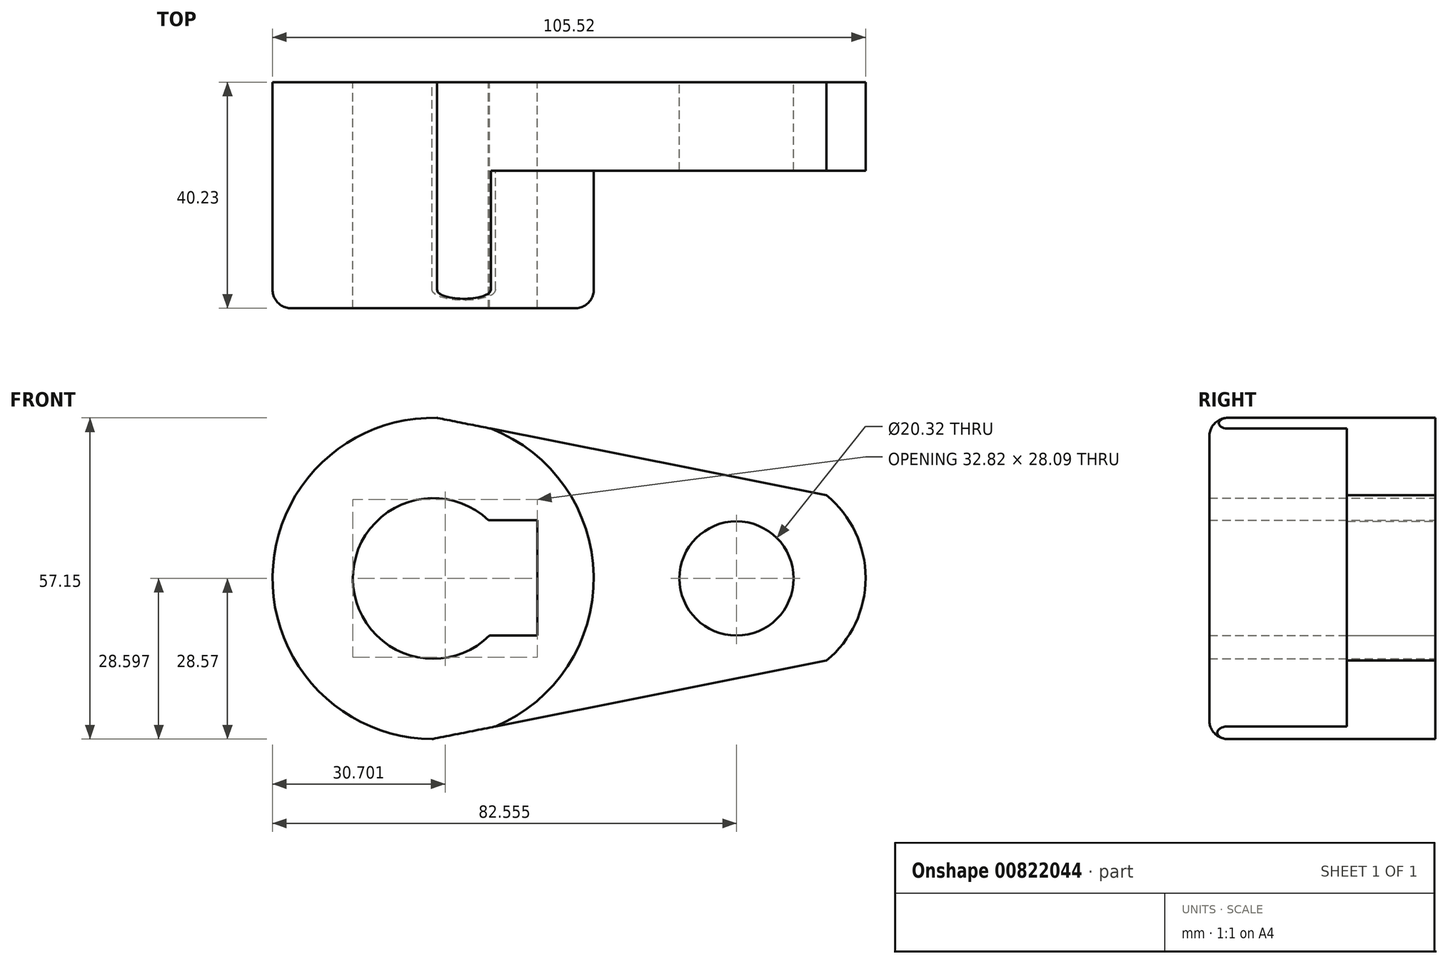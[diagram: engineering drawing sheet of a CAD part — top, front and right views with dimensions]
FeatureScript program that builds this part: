
annotation { "Feature Type Name" : "Feature", "Feature Type Description" : "" }
export const myFeature = defineFeature(function(context is Context, id is Id, definition is map)
    precondition{}
    {
        {
            var Q0;
            Q0=qCreatedBy(makeId("Front.planeOp"),FACE);
            var sketch = newSketch(context, id + "F0", { "sketchPlane" : qUnion([Q0])});
            skCircle(sketch, "E0", {"center": v(-57.07, 0) * mm, "radius": 28.58 * mm});
            skArc(sketch, "E1", {"start": v(-47.23, 10.36) * mm, "mid": v(-71.36, -0.15) * mm, "end": v(-47.02, -10.15) * mm});
            skLineSegment(sketch, "E2", {"start": v(-47.23, 10.36) * mm, "end": v(-38.54, 10.36) * mm});
            skLineSegment(sketch, "E3", {"start": v(-38.54, 10.36) * mm, "end": v(-38.54, -10.15) * mm});
            skLineSegment(sketch, "E4", {"start": v(-38.54, -10.15) * mm, "end": v(-47.02, -10.15) * mm});
            skCircle(sketch, "E5", {"center": v(-3.1, 0) * mm, "radius": 10.16 * mm});
            skLineSegment(sketch, "E6", {"start": v(-56.4, 28.57) * mm, "end": v(12.93, 14.8) * mm});
            skLineSegment(sketch, "E7", {"start": v(-57.24, -28.57) * mm, "end": v(12.93, -14.6) * mm});
            skLineSegment(sketch, "E8.trimOffspring", {"start": v(-3.5, -10.15) * mm, "end": v(-2.7, -10.15) * mm, "construction": true});
            skArc(sketch, "E9", {"start": v(12.93, -14.6) * mm, "mid": v(19.87, 0.1) * mm, "end": v(12.93, 14.8) * mm});
            skPoint(sketch, "E10.end.orphan", {"position": v(35.33, 10.36) * mm});
            skPoint(sketch, "E11.orphan", {"position": v(35.33, -10.15) * mm});
            skSolve(sketch);
        }
        {
            var Q0;
            {var subQ0=sQuery(id+"F0.wireOp",EDGE,"E6");var subQ1=sQuery(id+"F0.wireOp",EDGE,"E0");var subQ2=makeQuery(id+"F0.imprint","INTERSECT",VERTEX,{"disambiguationData":[OD(0.0)],"derivedFrom":[subQ1,subQ0]});Q0=makeQuery(id+"F0.imprint","IMPRINT",FACE,{"disambiguationData":[TD([[makeQuery(id+"F0.imprint","IMPRINT",EDGE,{"disambiguationData":[TD([[subQ2,1.0]])],"derivedFrom":subQ1}),1.0]])]});}
            var Q1;
            {var subQ0=sQuery(id+"F0.wireOp",EDGE,"E7");var subQ1=sQuery(id+"F0.wireOp",EDGE,"E0");var subQ2=makeQuery(id+"F0.imprint","INTERSECT",VERTEX,{"disambiguationData":[OD(0.0)],"derivedFrom":[subQ1,subQ0]});Q1=makeQuery(id+"F0.imprint","IMPRINT",FACE,{"disambiguationData":[TD([[makeQuery(id+"F0.imprint","IMPRINT",EDGE,{"disambiguationData":[TD([[subQ2,-1.0]])],"derivedFrom":subQ1}),1.0]])]});}
            var Q2;
            Q2=makeQuery(id+"F0.imprint","IMPRINT",FACE,{"disambiguationData":[TD([[makeQuery(id+"F0.imprint","IMPRINT",EDGE,{"derivedFrom":sQuery(id+"F0.wireOp",EDGE,"E1")}),-1.0]])]});
            extrude(context, id + "F1", {"entities" : qUnion([Q0, Q1, Q2]), "depth" : 40.23 * mm, "offsetDistance" : 25.4 * mm});
        }
        {
            var Q0;
            Q0=makeQuery(id+"F0.imprint","IMPRINT",FACE,{"disambiguationData":[TD([[makeQuery(id+"F0.imprint","IMPRINT",EDGE,{"derivedFrom":sQuery(id+"F0.wireOp",EDGE,"E5")}),-1.0]])]});
            extrude(context, id + "F2", {"entities" : qUnion([Q0]), "operationType" : NewBodyOperationType.ADD, "depth" : 15.77 * mm, "offsetDistance" : 25.4 * mm});
        }
        {
            var Q0;
            Q0=makeQuery(id+"F1.opExtrude","CAP_EDGE",EDGE,{"disambiguationData":[OSD([sQuery(id+"F0.wireOp",EDGE,"E0")])],"isStart":false});
            fillet(context, id + "F3", {"entities" : qUnion([Q0]), "radius" : 3.3 * mm, "tangentPropagation" : true, "allowEdgeOverflow" : false});
        }
    });
